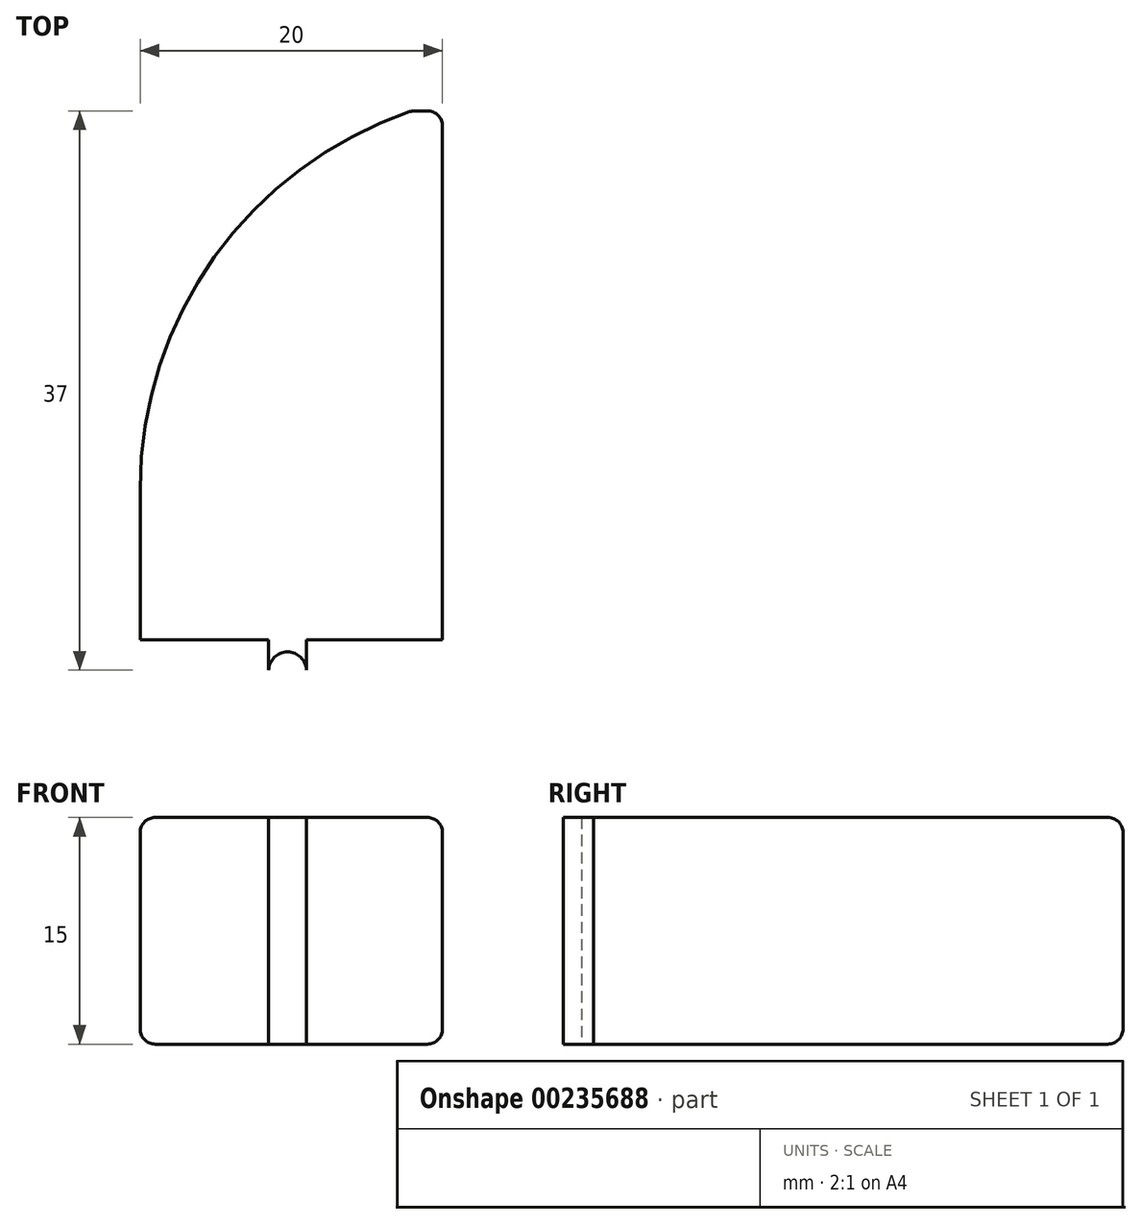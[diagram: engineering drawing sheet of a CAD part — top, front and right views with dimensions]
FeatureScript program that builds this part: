
annotation { "Feature Type Name" : "Feature", "Feature Type Description" : "" }
export const myFeature = defineFeature(function(context is Context, id is Id, definition is map)
    precondition{}
    {
        {
            var Q0;
            Q0=qCreatedBy(makeId("Front.planeOp"),FACE);
            var sketch = newSketch(context, id + "F0", { "sketchPlane" : qUnion([Q0])});
            skLineSegment(sketch, "E0.bottom", {"start": v(0, 0) * mm, "end": v(-20, 0) * mm});
            skLineSegment(sketch, "E0.top", {"start": v(0, 15) * mm, "end": v(-20, 15) * mm});
            skLineSegment(sketch, "E0.left", {"start": v(0, 0) * mm, "end": v(0, 15) * mm});
            skLineSegment(sketch, "E0.right", {"start": v(-20, 0) * mm, "end": v(-20, 15) * mm});
            skSolve(sketch);
        }
        {
            var Q0;
            Q0 = qSketchRegion(id + "F0", true);
            extrude(context, id + "F1", {"entities" : qUnion([Q0]), "depth" : 10 * mm});
        }
        {
            var Q0;
            Q0=makeQuery(id+"F1.opExtrude","SWEPT_EDGE",EDGE,{"disambiguationData":[OSD([sQuery(id+"F0.wireOp",EDGE,"E0.top"),sQuery(id+"F0.wireOp",EDGE,"E0.right")])]});
            var Q1;
            Q1=makeQuery(id+"F1.opExtrude","SWEPT_EDGE",EDGE,{"disambiguationData":[OSD([sQuery(id+"F0.wireOp",EDGE,"E0.top"),sQuery(id+"F0.wireOp",EDGE,"E0.left")])]});
            var Q2;
            Q2=makeQuery(id+"F1.opExtrude","SWEPT_EDGE",EDGE,{"disambiguationData":[OSD([sQuery(id+"F0.wireOp",EDGE,"E0.bottom"),sQuery(id+"F0.wireOp",EDGE,"E0.right")])]});
            var Q3;
            Q3=makeQuery(id+"F1.opExtrude","SWEPT_EDGE",EDGE,{"disambiguationData":[OSD([sQuery(id+"F0.wireOp",EDGE,"E0.bottom"),sQuery(id+"F0.wireOp",EDGE,"E0.left")])]});
            fillet(context, id + "F2", {"entities" : qUnion([Q0, Q1, Q2, Q3]), "radius" : 1 * mm, "tangentPropagation" : true, "allowEdgeOverflow" : false});
        }
        {
            var Q0;
            Q0=qCreatedBy(makeId("Top.planeOp"),FACE);
            var sketch = newSketch(context, id + "F3", { "sketchPlane" : qUnion([Q0])});
            skLineSegment(sketch, "E1.0", {"start": v(0, 0) * mm, "end": v(-20, 0) * mm});
            skArc(sketch, "E2", {"start": v(-2, 25) * mm, "mid": v(-15.03, 15.4) * mm, "end": v(-20, 0) * mm});
            skLineSegment(sketch, "E3", {"start": v(0, 0) * mm, "end": v(0, 25) * mm});
            skLineSegment(sketch, "E4", {"start": v(0, 25) * mm, "end": v(-2, 25) * mm});
            skSolve(sketch);
        }
        {
            var Q0;
            Q0 = qSketchRegion(id + "F3", true);
            extrude(context, id + "F4", {"entities" : qUnion([Q0]), "operationType" : NewBodyOperationType.ADD, "depth" : 15 * mm});
        }
        {
            var Q0;
            Q0=makeQuery(id+"F4.opExtrude","CAP_EDGE",EDGE,{"disambiguationData":[OSD([sQuery(id+"F3.wireOp",EDGE,"E2")])],"isStart":false});
            var Q1;
            Q1=makeQuery(id+"F4.opExtrude","CAP_EDGE",EDGE,{"disambiguationData":[OSD([sQuery(id+"F3.wireOp",EDGE,"E3")])],"isStart":false});
            var Q2;
            Q2=makeQuery(id+"F4.opExtrude","CAP_EDGE",EDGE,{"disambiguationData":[OSD([sQuery(id+"F3.wireOp",EDGE,"E4")])],"isStart":false});
            var Q3;
            Q3=makeQuery(id+"F4.opExtrude","CAP_EDGE",EDGE,{"disambiguationData":[OSD([sQuery(id+"F3.wireOp",EDGE,"E3")])],"isStart":true});
            var Q4;
            Q4=makeQuery(id+"F4.opExtrude","CAP_EDGE",EDGE,{"disambiguationData":[OSD([sQuery(id+"F3.wireOp",EDGE,"E4")])],"isStart":true});
            var Q5;
            Q5=makeQuery(id+"F4.opExtrude","CAP_EDGE",EDGE,{"disambiguationData":[OSD([sQuery(id+"F3.wireOp",EDGE,"E2")])],"isStart":true});
            fillet(context, id + "F5", {"entities" : qUnion([Q0, Q1, Q2, Q3, Q4, Q5]), "radius" : 1 * mm, "tangentPropagation" : true, "allowEdgeOverflow" : false});
        }
        {
            var Q0;
            Q0=makeQuery(id+"F4.opExtrude","SWEPT_EDGE",EDGE,{"disambiguationData":[OSD([sQuery(id+"F3.wireOp",EDGE,"E2"),sQuery(id+"F3.wireOp",EDGE,"E4")])]});
            fillet(context, id + "F6", {"entities" : qUnion([Q0]), "radius" : 1 * mm, "tangentPropagation" : true, "allowEdgeOverflow" : false});
        }
        {
            var Q0;
            Q0=makeQuery(id+"F4.opExtrude","SWEPT_EDGE",EDGE,{"disambiguationData":[OSD([sQuery(id+"F3.wireOp",EDGE,"E3"),sQuery(id+"F3.wireOp",EDGE,"E4")])]});
            fillet(context, id + "F7", {"entities" : qUnion([Q0]), "radius" : 1 * mm, "tangentPropagation" : true, "allowEdgeOverflow" : false});
        }
        {
            var Q0;
            Q0=qCreatedBy(makeId("Top.planeOp"),FACE);
            var sketch = newSketch(context, id + "F8", { "sketchPlane" : qUnion([Q0])});
            skLineSegment(sketch, "E5.bottom", {"start": v(-11.5, -10) * mm, "end": v(-9, -10) * mm});
            skLineSegment(sketch, "E5.left", {"start": v(-11.5, -10) * mm, "end": v(-11.5, -12) * mm});
            skLineSegment(sketch, "E5.right", {"start": v(-9, -10) * mm, "end": v(-9, -12) * mm});
            skArc(sketch, "E6", {"start": v(-9, -12) * mm, "mid": v(-10.25, -10.8) * mm, "end": v(-11.5, -12) * mm});
            skSolve(sketch);
        }
        {
            var Q0;
            Q0=makeQuery(id+"F8.imprint","IMPRINT",FACE,{"disambiguationData":[TD([[makeQuery(id+"F8.imprint","IMPRINT",EDGE,{"derivedFrom":sQuery(id+"F8.wireOp",EDGE,"E5.bottom")}),-1.0]])]});
            var Q1;
            Q1=makeQuery(id+"F4.boolean.opBoolean","MERGE",FACE,{"derivedFrom":[makeQuery(id+"F1.opExtrude","SWEPT_FACE",FACE,{"disambiguationData":[OSD([sQuery(id+"F0.wireOp",EDGE,"E0.top")])]}),makeQuery(id+"F4.opExtrude","CAP_FACE",FACE,{"disambiguationData":[OSD([sQuery(id+"F3.wireOp",EDGE,"E1.0"),sQuery(id+"F3.wireOp",EDGE,"E2"),sQuery(id+"F3.wireOp",EDGE,"E3"),sQuery(id+"F3.wireOp",EDGE,"E4")])],"isStart":false})]});
            extrude(context, id + "F9", {"entities" : qUnion([Q0]), "operationType" : NewBodyOperationType.ADD, "endBound" : BoundingType.UP_TO_SURFACE, "depth" : 25 * mm, "endBoundEntityFace" : qUnion([Q1]), "offsetDistance" : 25 * mm});
        }
    });
